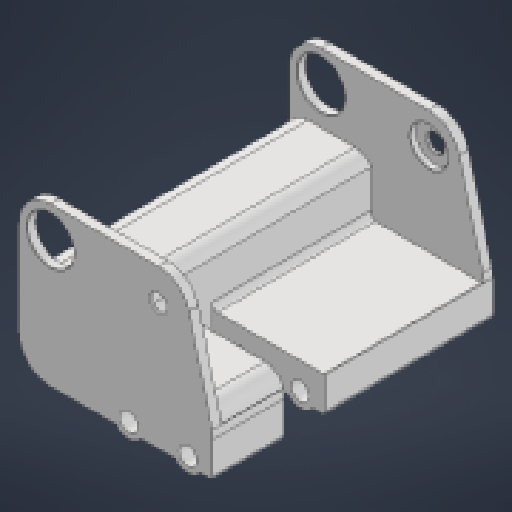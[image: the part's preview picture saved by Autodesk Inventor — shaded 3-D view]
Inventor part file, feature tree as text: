
AUTODESK INVENTOR PART (.ipt)
format: ipt  version: 2024.1 (Build 281209000, 209)  size: 363,008 bytes
history: native  units: in
note: dims shown in document units (in); Inventor stores cm internally (conversion verified against a paired STEP export)
features: extrude x10, sketch x9, reference x9, projected_geometry x5, other x4, chamfer x3, fillet x1
ambient origin geometry x8: Origin, YZ Plane, XZ Plane, XY Plane, X Axis, Y Axis, Z Axis, Center Point
bodies: Solid1 (feature_tree)
feature tree (41):
  extrude  "Extrusion1"  Depth=0.12in
  extrude  "Extrusion2"  Depth=0.42in
  chamfer  "Chamfer1"  Distance=0.0625in
  extrude  "Extrusion3"  Depth=0.0417in TaperAngle=0.0deg
  fillet  "Fillet1"  Radius=0.41in
  extrude  "Extrusion4"  Depth=0.125in
  extrude  "Extrusion5"  Depth=0.276in TaperAngle=0.0deg
  extrude  "Extrusion6"  Depth=0.0625in TaperAngle=0.0deg
  extrude  "Extrusion7"  Depth=0.125in TaperAngle=45.0deg
  chamfer  "Chamfer2"  Distance=0.12in
  sketch  "Sketch8"  dims[d20=1.0545in d21=0.0in d22=0.0625in d23=0.0in]
  extrude  "Extrusion8"  Depth=0.125in
  extrude  "Extrusion9"  Depth=0.125in
  extrude  "Extrusion10"  Depth=0.125in
  chamfer  "Chamfer3"  Distance=0.0417in
  sketch  "Sketch1"  dims[d0=0.005in d1=0.12in]
  reference  "Reference1"
  reference  "Reference2"
  reference  "Reference3"
  sketch  "Sketch2"  dims[d2=0.42in d3=0.42in]
  sketch  "Sketch3"  dims[d4=0.42in d5=0.0625in d6=0.0in]
  reference  "Reference4"
  projected_geometry  "Projected Loop1"
  reference  "Reference5"
  sketch  "Sketch4"  dims[d7=0.25in d8=0.0417in d9=0.0in]
  reference  "Reference6"
  projected_geometry  "Projected Loop2"
  sketch  "Sketch5"  dims[d10=0.005in d11=0.125in d12=45.0deg d13=0.41in d14=0.0in]
  reference  "Reference7"
  projected_geometry  "Projected Loop3"
  projected_geometry  "Projected Loop4"
  reference  "Reference8"
  sketch  "Sketch6"  dims[d15=0.125in d16=0.25in]
  projected_geometry  "Projected Loop5"
  sketch  "Sketch7"  dims[d17=0.005in d18=0.276in d19=0.0in]
  reference  "Reference9"
  sketch  "Sketch9"  dims[d24=0.0417in d25=0.0in d26=0.005in d27=0.125in d28=45.0deg d29=0.12in d30=0.2in d31=0.12in d32=0.2in d33=0.0417in d34=0.0in d35=1.0in d36=0.0in d37=0.3in d38=0.0in d39=0.005in d40=0.125in d41=45.0deg]
  other  "<userpath>\Documents\School\FallCAD\Bio\Bio.iam"
  other  "Bio.iam"
  other  "Bio12tNew:1"
  other  "Servo HS425BB:1"
